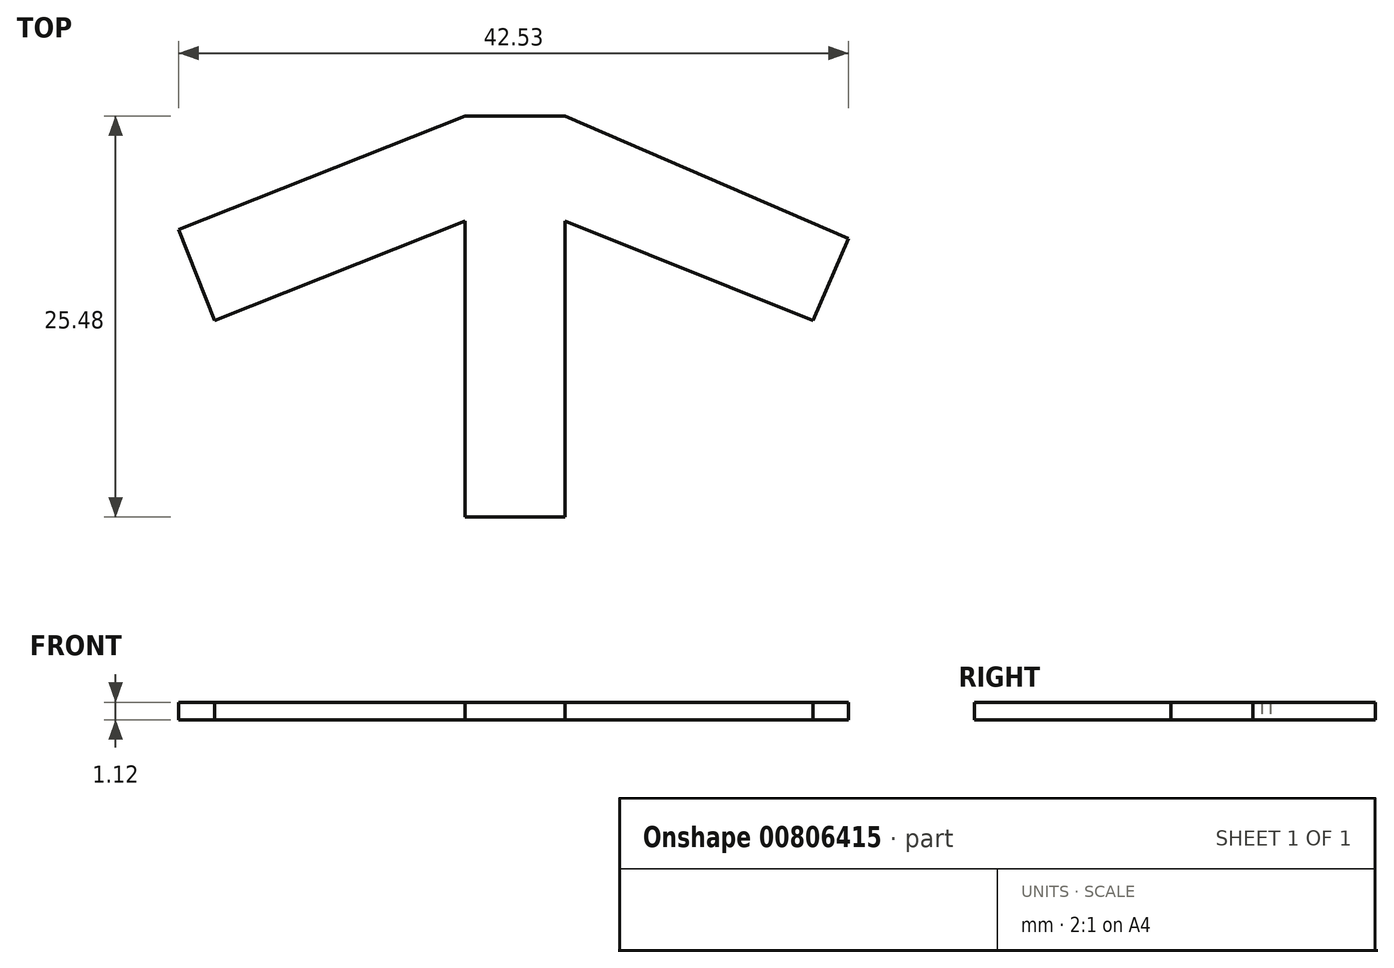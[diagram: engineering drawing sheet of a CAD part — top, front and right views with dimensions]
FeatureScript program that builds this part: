
annotation { "Feature Type Name" : "Feature", "Feature Type Description" : "" }
export const myFeature = defineFeature(function(context is Context, id is Id, definition is map)
    precondition{}
    {
        {
            var Q0;
            Q0=qCreatedBy(makeId("Top.planeOp"),FACE);
            var sketch = newSketch(context, id + "F0", { "sketchPlane" : qUnion([Q0])});
            skLineSegment(sketch, "E0.bottom", {"start": v(-3.28, 7.21) * mm, "end": v(3.1, 7.21) * mm});
            skLineSegment(sketch, "E0.top", {"start": v(-3.28, -18.27) * mm, "end": v(3.1, -18.27) * mm});
            skLineSegment(sketch, "E0.left", {"start": v(-3.28, 7.21) * mm, "end": v(-3.28, -18.27) * mm});
            skLineSegment(sketch, "E0.right", {"start": v(3.1, 7.21) * mm, "end": v(3.1, -18.27) * mm});
            skLineSegment(sketch, "E1", {"start": v(-3.28, 7.21) * mm, "end": v(-21.45, 0) * mm});
            skLineSegment(sketch, "E2", {"start": v(-21.45, 0) * mm, "end": v(-19.16, -5.77) * mm});
            skLineSegment(sketch, "E3", {"start": v(-19.16, -5.77) * mm, "end": v(-3.28, 0.53) * mm});
            skLineSegment(sketch, "E4", {"start": v(3.1, 7.21) * mm, "end": v(21.08, -0.58) * mm});
            skLineSegment(sketch, "E5", {"start": v(21.08, -0.58) * mm, "end": v(18.83, -5.77) * mm});
            skLineSegment(sketch, "E6", {"start": v(18.83, -5.77) * mm, "end": v(3.1, 0.53) * mm});
            skSolve(sketch);
        }
        {
            var Q0;
            {var subQ0=sQuery(id+"F0.wireOp",EDGE,"E1");Q0=makeQuery(id+"F0.imprint","IMPRINT",FACE,{"disambiguationData":[TD([[makeQuery(id+"F0.imprint","IMPRINT",EDGE,{"derivedFrom":subQ0}),1.0]])]});}
            var Q1;
            {var subQ3=sQuery(id+"F0.wireOp",EDGE,"E0.bottom");Q1=makeQuery(id+"F0.imprint","IMPRINT",FACE,{"disambiguationData":[TD([[makeQuery(id+"F0.imprint","IMPRINT",EDGE,{"derivedFrom":subQ3}),-1.0]])]});}
            var Q2;
            {var subQ0=sQuery(id+"F0.wireOp",EDGE,"E4");Q2=makeQuery(id+"F0.imprint","IMPRINT",FACE,{"disambiguationData":[TD([[makeQuery(id+"F0.imprint","IMPRINT",EDGE,{"derivedFrom":subQ0}),-1.0]])]});}
            extrude(context, id + "F1", {"entities" : qUnion([Q0, Q1, Q2]), "depth" : 1.12 * mm, "offsetDistance" : 25.4 * mm});
        }
    });
